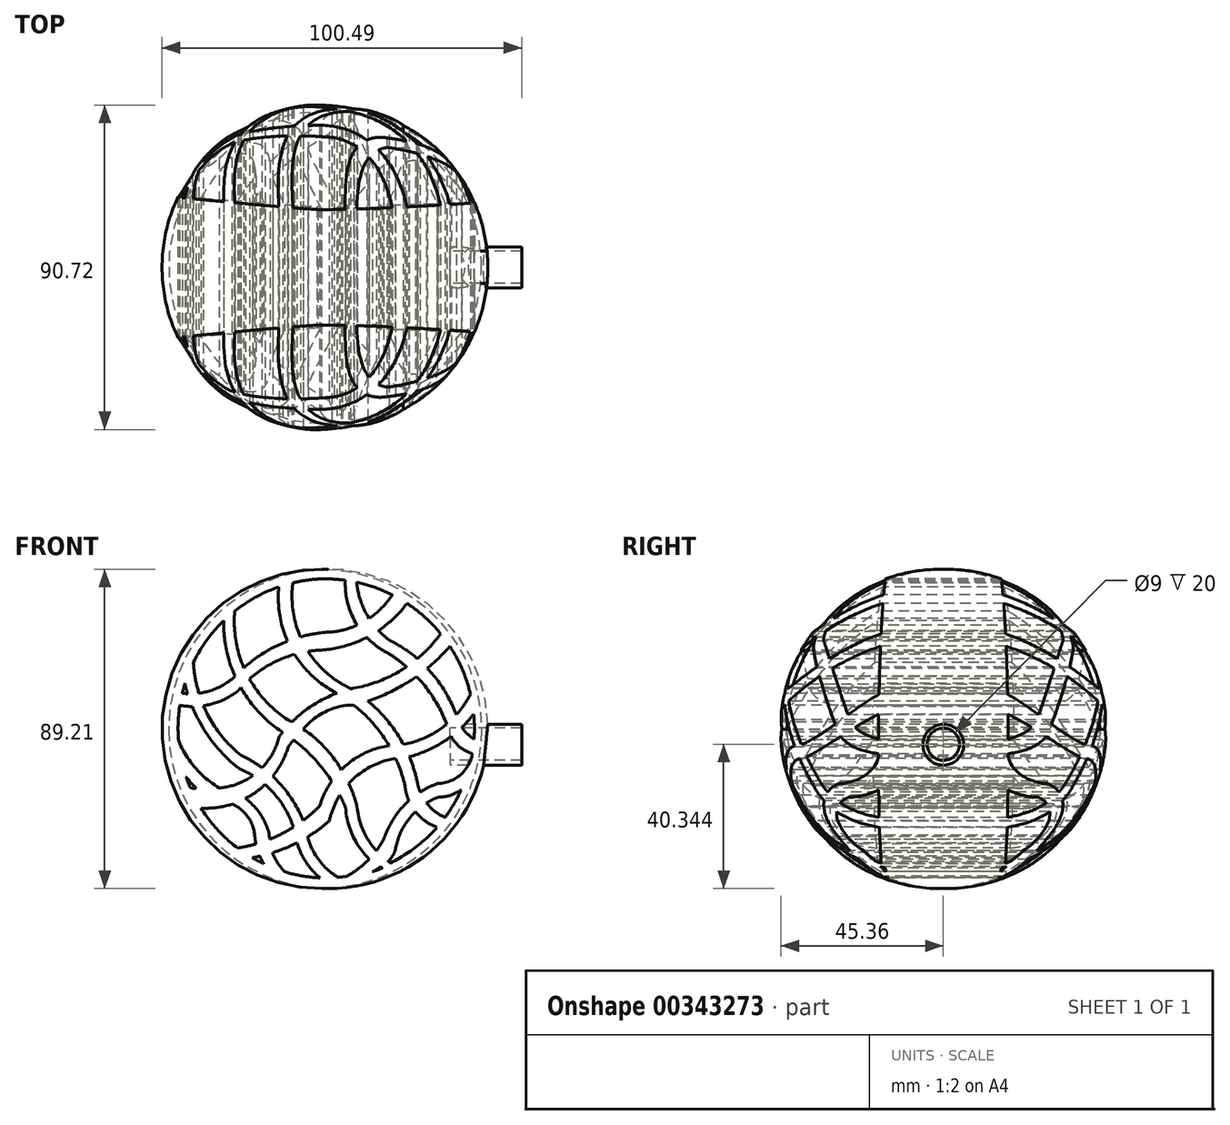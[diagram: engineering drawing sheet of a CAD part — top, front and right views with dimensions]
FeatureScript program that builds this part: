
annotation { "Feature Type Name" : "Feature", "Feature Type Description" : "" }
export const myFeature = defineFeature(function(context is Context, id is Id, definition is map)
    precondition{}
    {
        {
            var Q0;
            Q0=qCreatedBy(makeId("Front.planeOp"),FACE);
            var sketch = newSketch(context, id + "F0", { "sketchPlane" : qUnion([Q0])});
            skArc(sketch, "E0", {"start": v(-34.98, -55.53) * mm, "mid": v(10.54, -10.93) * mm, "end": v(-34.98, 33.67) * mm});
            skLineSegment(sketch, "E1", {"start": v(-34.98, 33.67) * mm, "end": v(-34.98, -55.53) * mm});
            skSolve(sketch);
        }
        {
            var Q0;
            Q0=makeQuery(id+"F0.imprint","IMPRINT",FACE,{"disambiguationData":[TD([[makeQuery(id+"F0.imprint","IMPRINT",EDGE,{"derivedFrom":sQuery(id+"F0.wireOp",EDGE,"E0")}),1.0]])]});
            var Q1;
            Q1=sQuery(id+"F0.wireOp",EDGE,"E1");
            revolve(context, id + "F1", {"entities" : qUnion([Q0]), "axis" : qUnion([Q1]), "revolveType" : RevolveType.FULL});
        }
        {
            var Q0;
            Q0=qCreatedBy(makeId("Front.planeOp"),FACE);
            var sketch = newSketch(context, id + "F2", { "sketchPlane" : qUnion([Q0])});
            skArc(sketch, "E2", {"start": v(-36.98, 31.45) * mm, "mid": v(-40.71, 31.04) * mm, "end": v(-44.39, 30.3) * mm});
            skArc(sketch, "E3", {"start": v(-37.25, -53) * mm, "mid": v(-36.08, -53.04) * mm, "end": v(-34.91, -53.06) * mm});
            skArc(sketch, "E4", {"start": v(-9.49, -26.67) * mm, "mid": v(-10.57, -22.44) * mm, "end": v(-12.1, -18.35) * mm});
            skArc(sketch, "E5", {"start": v(-9.49, -26.67) * mm, "mid": v(-9.1, -28.02) * mm, "end": v(-8.57, -29.33) * mm});
            skArc(sketch, "E6", {"start": v(-44.39, 30.3) * mm, "mid": v(-44.42, 22.07) * mm, "end": v(-42.13, 14.17) * mm});
            skPoint(sketch, "E7.end.orphan", {"position": v(-32.31, 0) * mm});
            skArc(sketch, "E8", {"start": v(-47.27, 29.48) * mm, "mid": v(-47.15, 21.22) * mm, "end": v(-44.74, 13.3) * mm});
            skArc(sketch, "E9", {"start": v(-12.1, -26.66) * mm, "mid": v(-13.32, -22.55) * mm, "end": v(-14.95, -18.58) * mm});
            skArc(sketch, "E10", {"start": v(-12.1, -26.66) * mm, "mid": v(-11.7, -28.95) * mm, "end": v(-10.9, -31.12) * mm});
            skArc(sketch, "E11", {"start": v(-60.68, 22.25) * mm, "mid": v(-60.35, 13.59) * mm, "end": v(-57.8, 5.3) * mm});
            skArc(sketch, "E12", {"start": v(-26.5, -32.73) * mm, "mid": v(-27.54, -29.33) * mm, "end": v(-28.9, -26.06) * mm});
            skArc(sketch, "E13", {"start": v(-26.5, -32.73) * mm, "mid": v(-24.64, -39.73) * mm, "end": v(-20.58, -45.73) * mm});
            skArc(sketch, "E14", {"start": v(-62.74, 20.49) * mm, "mid": v(-62.14, 11.87) * mm, "end": v(-59.5, 3.64) * mm});
            skArc(sketch, "E15", {"start": v(-28.74, -32.73) * mm, "mid": v(-29.7, -30.56) * mm, "end": v(-30.77, -28.45) * mm});
            skArc(sketch, "E16", {"start": v(-28.74, -32.73) * mm, "mid": v(-26.7, -40.64) * mm, "end": v(-21.92, -47.29) * mm});
            skArc(sketch, "E17", {"start": v(-72.25, 7.8) * mm, "mid": v(-71.71, 3.08) * mm, "end": v(-70.56, -1.51) * mm});
            skArc(sketch, "E18", {"start": v(-41.33, -37.32) * mm, "mid": v(-45.02, -30.23) * mm, "end": v(-50.3, -24.22) * mm});
            skArc(sketch, "E19", {"start": v(-40.38, -40.83) * mm, "mid": v(-37.15, -47.76) * mm, "end": v(-31.5, -52.91) * mm});
            skArc(sketch, "E20", {"start": v(-74.01, 3.64) * mm, "mid": v(-73.41, 0.99) * mm, "end": v(-72.65, -1.62) * mm});
            skArc(sketch, "E21", {"start": v(-43.21, -38.6) * mm, "mid": v(-46.54, -31.57) * mm, "end": v(-51.74, -25.78) * mm});
            skArc(sketch, "E22", {"start": v(-42.48, -42) * mm, "mid": v(-39.62, -48.16) * mm, "end": v(-34.91, -53.06) * mm});
            skArc(sketch, "E23", {"start": v(-76.4, -14.3) * mm, "mid": v(-71.65, -22.1) * mm, "end": v(-64.61, -27.94) * mm});
            skArc(sketch, "E24", {"start": v(-75.14, -21.58) * mm, "mid": v(-72.79, -24.73) * mm, "end": v(-70.07, -27.58) * mm});
            skArc(sketch, "E25", {"start": v(-51.1, -40.4) * mm, "mid": v(-53.68, -34.67) * mm, "end": v(-58.24, -30.32) * mm});
            skArc(sketch, "E26", {"start": v(-51.1, -40.4) * mm, "mid": v(-51.04, -41.45) * mm, "end": v(-50.92, -42.48) * mm});
            skArc(sketch, "E27", {"start": v(-54.11, -40.57) * mm, "mid": v(-56.23, -35.03) * mm, "end": v(-60.9, -31.4) * mm});
            skArc(sketch, "E28", {"start": v(-54.11, -40.57) * mm, "mid": v(-53.93, -42) * mm, "end": v(-53.65, -43.41) * mm});
            skArc(sketch, "E29", {"start": v(-28.76, 31.04) * mm, "mid": v(-28.08, 24.17) * mm, "end": v(-25.23, 17.88) * mm});
            skArc(sketch, "E30", {"start": v(-0.36, -9.76) * mm, "mid": v(-4.1, -2.21) * mm, "end": v(-9.3, 4.4) * mm});
            skArc(sketch, "E31", {"start": v(0.5, -12.2) * mm, "mid": v(3.02, -15.57) * mm, "end": v(6.77, -17.47) * mm});
            skArc(sketch, "E32", {"start": v(-26.71, 30.69) * mm, "mid": v(-25.48, 24.72) * mm, "end": v(-22.78, 19.26) * mm});
            skArc(sketch, "E33", {"start": v(1.51, -8) * mm, "mid": v(-2, -0.48) * mm, "end": v(-7.1, 6.07) * mm});
            skArc(sketch, "E34", {"start": v(2.63, -10.39) * mm, "mid": v(4.6, -12.8) * mm, "end": v(7.13, -14.62) * mm});
            skArc(sketch, "E35", {"start": v(-35.98, 11.62) * mm, "mid": v(-29.38, 12.78) * mm, "end": v(-23.17, 15.27) * mm});
            skArc(sketch, "E36", {"start": v(-35.98, 11.62) * mm, "mid": v(-38.26, 11.45) * mm, "end": v(-40.52, 11.12) * mm});
            skArc(sketch, "E37", {"start": v(-75.96, -3.74) * mm, "mid": v(-73.85, -4.06) * mm, "end": v(-71.73, -4.15) * mm});
            skArc(sketch, "E38", {"start": v(-32.4, 15.7) * mm, "mid": v(-28.73, 16.5) * mm, "end": v(-25.23, 17.88) * mm});
            skArc(sketch, "E39", {"start": v(-32.4, 15.7) * mm, "mid": v(-37.31, 15.24) * mm, "end": v(-42.13, 14.17) * mm});
            skArc(sketch, "E40", {"start": v(-75.5, -1.4) * mm, "mid": v(-74.07, -1.56) * mm, "end": v(-72.65, -1.62) * mm});
            skArc(sketch, "E41", {"start": v(-26.71, 0) * mm, "mid": v(-18.67, 2.33) * mm, "end": v(-11.34, 6.37) * mm});
            skArc(sketch, "E42", {"start": v(-26.71, 0) * mm, "mid": v(-27.29, -0.13) * mm, "end": v(-27.86, -0.28) * mm});
            skPoint(sketch, "E43.startSnap0", {"position": v(-71.16, -26.53) * mm});
            skArc(sketch, "E44", {"start": v(-70.56, -32.48) * mm, "mid": v(-65.67, -32.44) * mm, "end": v(-60.9, -31.4) * mm});
            skPoint(sketch, "E44.startSnap0", {"position": v(-6.54, -32.48) * mm});
            skArc(sketch, "E45", {"start": v(-26.71, -3.74) * mm, "mid": v(-26.71, -3.74) * mm, "end": v(-26.72, -3.74) * mm});
            skArc(sketch, "E46", {"start": v(-24, -2.97) * mm, "mid": v(-16.36, 0.14) * mm, "end": v(-9.3, 4.4) * mm});
            skArc(sketch, "E47", {"start": v(-59.5, -44.73) * mm, "mid": v(-56.55, -44.18) * mm, "end": v(-53.65, -43.41) * mm});
            skArc(sketch, "E48", {"start": v(-16.29, -15.99) * mm, "mid": v(-23.99, -18.32) * mm, "end": v(-30.45, -23.1) * mm});
            skArc(sketch, "E49", {"start": v(-13.32, -15.81) * mm, "mid": v(-6.43, -13.67) * mm, "end": v(-0.36, -9.76) * mm});
            skArc(sketch, "E50", {"start": v(-56.74, -46.61) * mm, "mid": v(-54.79, -46.29) * mm, "end": v(-52.85, -45.88) * mm});
            skArc(sketch, "E51", {"start": v(-14.95, -18.58) * mm, "mid": v(-22.58, -21.09) * mm, "end": v(-28.9, -26.06) * mm});
            skArc(sketch, "E52", {"start": v(-12.1, -18.35) * mm, "mid": v(-5.48, -15.95) * mm, "end": v(0.5, -12.2) * mm});
            skArc(sketch, "E53", {"start": v(-28.74, -52.6) * mm, "mid": v(-25.12, -50.22) * mm, "end": v(-21.92, -47.29) * mm});
            skPoint(sketch, "E53.endSnap0", {"position": v(-23.47, -41.94) * mm});
            skArc(sketch, "E54", {"start": v(-3.43, -26.67) * mm, "mid": v(-6.08, -27.85) * mm, "end": v(-8.57, -29.33) * mm});
            skArc(sketch, "E55", {"start": v(-3.43, -26.67) * mm, "mid": v(3.39, -23.97) * mm, "end": v(6.77, -17.47) * mm});
            skArc(sketch, "E56", {"start": v(-23.86, -51.57) * mm, "mid": v(-21.54, -50.67) * mm, "end": v(-19.44, -49.34) * mm});
            skArc(sketch, "E57", {"start": v(-3.43, -29.49) * mm, "mid": v(-5.43, -30.38) * mm, "end": v(-7.32, -31.48) * mm});
            skArc(sketch, "E58", {"start": v(-3.43, -29.49) * mm, "mid": v(0.88, -28.62) * mm, "end": v(4.45, -26.05) * mm});
            skArc(sketch, "E59.trimOffspring", {"start": v(-43.24, 10.5) * mm, "mid": v(-38.46, 4.54) * mm, "end": v(-32.31, 0) * mm});
            skArc(sketch, "E60.trimOffspring", {"start": v(-44.74, 13.3) * mm, "mid": v(-51.66, 9.95) * mm, "end": v(-57.8, 5.3) * mm});
            skArc(sketch, "E61.trimOffspring", {"start": v(-40.52, 11.12) * mm, "mid": v(-36.04, 5.47) * mm, "end": v(-30.3, 1.1) * mm});
            skArc(sketch, "E62.trimOffspring", {"start": v(-43.24, 10.5) * mm, "mid": v(-50.4, 7.61) * mm, "end": v(-56.7, 3.12) * mm});
            skArc(sketch, "E63.trimOffspring", {"start": v(-30.5, -1.07) * mm, "mid": v(-37.79, -4.56) * mm, "end": v(-44.1, -9.6) * mm});
            skArc(sketch, "E64.trimOffspring", {"start": v(-27.86, -0.28) * mm, "mid": v(-29.07, 0.43) * mm, "end": v(-30.3, 1.1) * mm});
            skArc(sketch, "E65.trimOffspring", {"start": v(-30.5, -1.07) * mm, "mid": v(-31.4, -0.52) * mm, "end": v(-32.31, 0) * mm});
            skArc(sketch, "E66.trimOffspring", {"start": v(-11.34, 6.37) * mm, "mid": v(-14.3, 8.77) * mm, "end": v(-17.45, 10.89) * mm});
            skArc(sketch, "E67.trimOffspring", {"start": v(-9.16, 8.02) * mm, "mid": v(-13.12, 11.06) * mm, "end": v(-17.45, 13.54) * mm});
            skArc(sketch, "E68.trimOffspring", {"start": v(-9.16, 8.02) * mm, "mid": v(-5.32, 11.62) * mm, "end": v(-2.02, 15.7) * mm});
            skArc(sketch, "E69.trimOffspring", {"start": v(-7.1, 6.07) * mm, "mid": v(-3.39, 9.36) * mm, "end": v(0, 12.98) * mm});
            skArc(sketch, "E70.trimOffspring", {"start": v(-23.17, 15.27) * mm, "mid": v(-20.5, 12.84) * mm, "end": v(-17.45, 10.89) * mm});
            skArc(sketch, "E71.trimOffspring", {"start": v(-22.78, 19.26) * mm, "mid": v(-18.95, 22.31) * mm, "end": v(-15.83, 26.08) * mm});
            skArc(sketch, "E72.trimOffspring", {"start": v(-20.8, 16.67) * mm, "mid": v(-19.2, 15.02) * mm, "end": v(-17.45, 13.54) * mm});
            skArc(sketch, "E73.trimOffspring", {"start": v(-20.8, 16.67) * mm, "mid": v(-16.1, 20.34) * mm, "end": v(-12.17, 24.82) * mm});
            skLineSegment(sketch, "E74", {"start": v(-15.83, 26.08) * mm, "end": v(-15.42, 26.7) * mm});
            skArc(sketch, "E75.trimOffspring", {"start": v(-28.76, 31.04) * mm, "mid": v(-32.86, 31.45) * mm, "end": v(-36.98, 31.45) * mm});
            skArc(sketch, "E76.trimOffspring", {"start": v(-15.42, 26.7) * mm, "mid": v(-20.92, 29.1) * mm, "end": v(-26.71, 30.69) * mm});
            skArc(sketch, "E77.trimOffspring", {"start": v(-2.02, 15.7) * mm, "mid": v(-6.72, 20.68) * mm, "end": v(-12.17, 24.82) * mm});
            skArc(sketch, "E78.trimOffspring", {"start": v(-47.27, 29.48) * mm, "mid": v(-54.3, 26.48) * mm, "end": v(-60.68, 22.25) * mm});
            skArc(sketch, "E79.trimOffspring", {"start": v(-62.74, 20.49) * mm, "mid": v(-68.1, 14.6) * mm, "end": v(-72.25, 7.8) * mm});
            skArc(sketch, "E80.trimOffspring", {"start": v(-74.01, 3.64) * mm, "mid": v(-74.83, 1.14) * mm, "end": v(-75.5, -1.4) * mm});
            skArc(sketch, "E81.trimOffspring", {"start": v(6.22, -1.28) * mm, "mid": v(3.77, 6.14) * mm, "end": v(0, 12.98) * mm});
            skArc(sketch, "E82.trimOffspring", {"start": v(2.63, -10.39) * mm, "mid": v(4.92, -8.04) * mm, "end": v(6.97, -5.48) * mm});
            skPoint(sketch, "E83.orphan", {"position": v(0, -10.77) * mm});
            skArc(sketch, "E84.trimOffspring", {"start": v(1.51, -8) * mm, "mid": v(4.13, -4.82) * mm, "end": v(6.22, -1.28) * mm});
            skArc(sketch, "E85.trimOffspring", {"start": v(6.6, -18.46) * mm, "mid": v(6.69, -17.96) * mm, "end": v(6.77, -17.47) * mm});
            skArc(sketch, "E86.trimOffspring", {"start": v(7.13, -14.62) * mm, "mid": v(7.3, -10.05) * mm, "end": v(6.97, -5.48) * mm});
            skArc(sketch, "E87.trimOffspring", {"start": v(-13.32, -15.81) * mm, "mid": v(-17.99, -8.83) * mm, "end": v(-24, -2.97) * mm});
            skArc(sketch, "E88.trimOffspring", {"start": v(-16.29, -15.99) * mm, "mid": v(-20.9, -9.36) * mm, "end": v(-26.72, -3.74) * mm});
            skArc(sketch, "E89.trimOffspring", {"start": v(-64.61, -27.94) * mm, "mid": v(-59.13, -26.7) * mm, "end": v(-54.23, -23.94) * mm});
            skPoint(sketch, "E43.start.orphan", {"position": v(-73.5, -26.53) * mm});
            skArc(sketch, "E90.trimOffspring", {"start": v(-58.24, -30.32) * mm, "mid": v(-54.8, -28.33) * mm, "end": v(-51.74, -25.78) * mm});
            skArc(sketch, "E91", {"start": v(-73.06, -27.58) * mm, "mid": v(-71.57, -28.05) * mm, "end": v(-70.07, -27.58) * mm});
            skArc(sketch, "E92.trimOffspring", {"start": v(-75.14, -21.58) * mm, "mid": v(-74.22, -24.62) * mm, "end": v(-73.06, -27.58) * mm});
            skArc(sketch, "E93.trimOffspring", {"start": v(-52.85, -45.88) * mm, "mid": v(-51.9, -47.88) * mm, "end": v(-50.7, -49.76) * mm});
            skArc(sketch, "E94.trimOffspring", {"start": v(-50.92, -42.48) * mm, "mid": v(-46.96, -40.74) * mm, "end": v(-43.21, -38.6) * mm});
            skArc(sketch, "E95.trimOffspring", {"start": v(-50.26, -45.18) * mm, "mid": v(-48.72, -48.45) * mm, "end": v(-46.49, -51.29) * mm});
            skArc(sketch, "E96.trimOffspring", {"start": v(-50.26, -45.18) * mm, "mid": v(-46.3, -43.78) * mm, "end": v(-42.48, -42) * mm});
            skArc(sketch, "E97.trimOffspring", {"start": v(-56.74, -46.61) * mm, "mid": v(-53.79, -48.3) * mm, "end": v(-50.7, -49.76) * mm});
            skPoint(sketch, "E98.orphan", {"position": v(-43.06, -39.1) * mm});
            skArc(sketch, "E99.trimOffspring", {"start": v(-41.33, -37.32) * mm, "mid": v(-38.56, -35.14) * mm, "end": v(-35.98, -32.73) * mm});
            skPoint(sketch, "E100.orphan", {"position": v(-40.72, -39.1) * mm});
            skArc(sketch, "E101.trimOffspring", {"start": v(-40.38, -40.83) * mm, "mid": v(-37.2, -38.74) * mm, "end": v(-34.22, -36.38) * mm});
            skArc(sketch, "E102.trimOffspring", {"start": v(-69.65, -4.02) * mm, "mid": v(-65.13, -12.08) * mm, "end": v(-58.73, -18.73) * mm});
            skArc(sketch, "E103.trimOffspring", {"start": v(-69.65, -4.02) * mm, "mid": v(-64.4, -2.69) * mm, "end": v(-59.7, 0) * mm});
            skArc(sketch, "E104.trimOffspring", {"start": v(-71.73, -4.15) * mm, "mid": v(-66.36, -13.71) * mm, "end": v(-58.73, -21.58) * mm});
            skArc(sketch, "E105.trimOffspring", {"start": v(-70.56, -1.51) * mm, "mid": v(-64.6, 0.15) * mm, "end": v(-59.5, 3.64) * mm});
            skArc(sketch, "E106.trimOffspring", {"start": v(-58.4, 1.45) * mm, "mid": v(-53.66, -5.3) * mm, "end": v(-47.52, -10.78) * mm});
            skArc(sketch, "E107.trimOffspring", {"start": v(-58.4, 1.45) * mm, "mid": v(-59.06, 0.73) * mm, "end": v(-59.7, 0) * mm});
            skArc(sketch, "E108.trimOffspring", {"start": v(-56.7, 3.12) * mm, "mid": v(-51.88, -3.54) * mm, "end": v(-45.58, -8.8) * mm});
            skArc(sketch, "E109.trimOffspring", {"start": v(-18, -48.03) * mm, "mid": v(-16.8, -46.51) * mm, "end": v(-15.83, -44.83) * mm});
            skArc(sketch, "E110.trimOffspring", {"start": v(-16.74, -48.92) * mm, "mid": v(-9.2, -44.28) * mm, "end": v(-2.78, -38.18) * mm});
            skArc(sketch, "E111.trimOffspring", {"start": v(-18, -48.03) * mm, "mid": v(-17.38, -48.49) * mm, "end": v(-16.74, -48.92) * mm});
            skArc(sketch, "E112.trimOffspring", {"start": v(-20.58, -45.73) * mm, "mid": v(-19.24, -43.89) * mm, "end": v(-18.06, -41.94) * mm});
            skArc(sketch, "E113.trimOffspring", {"start": v(-19.44, -49.34) * mm, "mid": v(-19.1, -49.58) * mm, "end": v(-18.74, -49.82) * mm});
            skArc(sketch, "E114.trimOffspring", {"start": v(-30.77, -28.45) * mm, "mid": v(-32.87, -32.26) * mm, "end": v(-34.22, -36.38) * mm});
            skArc(sketch, "E115.trimOffspring", {"start": v(-30.45, -23.1) * mm, "mid": v(-35.4, -16.47) * mm, "end": v(-41.71, -11.1) * mm});
            skArc(sketch, "E116.trimOffspring", {"start": v(-32.48, -25.55) * mm, "mid": v(-34.54, -28.99) * mm, "end": v(-35.98, -32.73) * mm});
            skArc(sketch, "E117.trimOffspring", {"start": v(-32.48, -25.55) * mm, "mid": v(-37.6, -18.92) * mm, "end": v(-43.81, -13.3) * mm});
            skArc(sketch, "E118.trimOffspring", {"start": v(-31.5, -52.91) * mm, "mid": v(-30.11, -52.77) * mm, "end": v(-28.74, -52.6) * mm});
            skArc(sketch, "E119.trimOffspring", {"start": v(-46.49, -51.29) * mm, "mid": v(-41.92, -52.4) * mm, "end": v(-37.25, -53) * mm});
            skArc(sketch, "E120.trimOffspring", {"start": v(-9.63, -33.28) * mm, "mid": v(-6.6, -36.29) * mm, "end": v(-2.78, -38.18) * mm});
            skArc(sketch, "E121.trimOffspring", {"start": v(-9.63, -33.28) * mm, "mid": v(-13.73, -38.52) * mm, "end": v(-15.83, -44.83) * mm});
            skArc(sketch, "E122.trimOffspring", {"start": v(-7.32, -31.48) * mm, "mid": v(-4.63, -34.31) * mm, "end": v(-1.24, -36.26) * mm});
            skArc(sketch, "E123.trimOffspring", {"start": v(-10.9, -31.12) * mm, "mid": v(-15.21, -36.05) * mm, "end": v(-18.06, -41.94) * mm});
            skArc(sketch, "E124.trimOffspring", {"start": v(-75.96, -3.74) * mm, "mid": v(-76.5, -9) * mm, "end": v(-76.4, -14.3) * mm});
            skArc(sketch, "E125.trimOffspring", {"start": v(-44.1, -9.6) * mm, "mid": v(-44.84, -9.2) * mm, "end": v(-45.58, -8.8) * mm});
            skArc(sketch, "E126.trimOffspring", {"start": v(-43.81, -13.3) * mm, "mid": v(-44.8, -14.53) * mm, "end": v(-45.73, -15.81) * mm});
            skArc(sketch, "E127.trimOffspring", {"start": v(-46.03, -11.73) * mm, "mid": v(-46.77, -11.25) * mm, "end": v(-47.52, -10.78) * mm});
            skArc(sketch, "E128.trimOffspring", {"start": v(-46.03, -11.73) * mm, "mid": v(-46.66, -12.5) * mm, "end": v(-47.27, -13.28) * mm});
            skArc(sketch, "E129", {"start": v(-26.71, -3.74) * mm, "mid": v(-35.08, -5.64) * mm, "end": v(-41.71, -11.1) * mm});
            skArc(sketch, "E130.trimOffspring", {"start": v(-1.24, -36.26) * mm, "mid": v(1.96, -31.35) * mm, "end": v(4.45, -26.05) * mm});
            skArc(sketch, "E131.trimOffspring", {"start": v(-52.49, -22.42) * mm, "mid": v(-49.24, -18.21) * mm, "end": v(-47.27, -13.28) * mm});
            skArc(sketch, "E132.trimOffspring", {"start": v(-52.49, -22.42) * mm, "mid": v(-55.5, -20.4) * mm, "end": v(-58.73, -18.73) * mm});
            skArc(sketch, "E133.trimOffspring", {"start": v(-50.3, -24.22) * mm, "mid": v(-47.58, -20.25) * mm, "end": v(-45.73, -15.81) * mm});
            skArc(sketch, "E134.trimOffspring", {"start": v(-54.23, -23.94) * mm, "mid": v(-56.42, -22.65) * mm, "end": v(-58.73, -21.58) * mm});
            skArc(sketch, "E135.trimOffspring", {"start": v(-70.56, -32.48) * mm, "mid": v(-65.63, -39.15) * mm, "end": v(-59.5, -44.73) * mm});
            skArc(sketch, "E136.trimOffspring", {"start": v(-23.86, -51.57) * mm, "mid": v(-21.27, -50.77) * mm, "end": v(-18.74, -49.82) * mm});
            skSolve(sketch);
        }
        {
            var Q0;
            Q0=qCreatedBy(makeId("Front.planeOp"),FACE);
            var sketch = newSketch(context, id + "F3", { "sketchPlane" : qUnion([Q0])});
            skArc(sketch, "E137.0", {"start": v(-36.95, 30.95) * mm, "mid": v(-40.47, 30.57) * mm, "end": v(-43.94, 29.9) * mm});
            skArc(sketch, "E137.1", {"start": v(-32.45, 16.21) * mm, "mid": v(-37.19, 15.78) * mm, "end": v(-41.84, 14.78) * mm});
            skArc(sketch, "E137.2", {"start": v(-32.45, 16.21) * mm, "mid": v(-29.14, 16.92) * mm, "end": v(-25.97, 18.1) * mm});
            skArc(sketch, "E137.3", {"start": v(-43.94, 29.9) * mm, "mid": v(-43.92, 22.2) * mm, "end": v(-41.84, 14.78) * mm});
            skArc(sketch, "E137.4", {"start": v(-29.3, 30.6) * mm, "mid": v(-28.58, 24.1) * mm, "end": v(-25.97, 18.1) * mm});
            skArc(sketch, "E137.5", {"start": v(-29.3, 30.6) * mm, "mid": v(-33.11, 30.95) * mm, "end": v(-36.95, 30.95) * mm});
            skArc(sketch, "E138.0", {"start": v(-26.14, 30.05) * mm, "mid": v(-24.97, 24.8) * mm, "end": v(-22.63, 19.96) * mm});
            skArc(sketch, "E138.1", {"start": v(-16.16, 26.51) * mm, "mid": v(-21.04, 28.6) * mm, "end": v(-26.14, 30.05) * mm});
            skLineSegment(sketch, "E138.2", {"start": v(-16.26, 26.37) * mm, "end": v(-16.16, 26.51) * mm});
            skArc(sketch, "E138.3", {"start": v(-22.63, 19.96) * mm, "mid": v(-19.13, 22.85) * mm, "end": v(-16.26, 26.37) * mm});
            skArc(sketch, "E139.0", {"start": v(-2.65, 15.68) * mm, "mid": v(-7.03, 20.27) * mm, "end": v(-12.04, 24.14) * mm});
            skArc(sketch, "E139.1", {"start": v(-20.02, 16.57) * mm, "mid": v(-15.71, 20.01) * mm, "end": v(-12.04, 24.14) * mm});
            skArc(sketch, "E139.2", {"start": v(-9.15, 8.69) * mm, "mid": v(-5.68, 11.98) * mm, "end": v(-2.65, 15.68) * mm});
            skArc(sketch, "E139.3", {"start": v(-9.15, 8.69) * mm, "mid": v(-13, 11.59) * mm, "end": v(-17.18, 13.97) * mm});
            skArc(sketch, "E139.4", {"start": v(-20.02, 16.57) * mm, "mid": v(-18.65, 15.21) * mm, "end": v(-17.18, 13.97) * mm});
            skArc(sketch, "E140.0", {"start": v(-35.95, 11.1) * mm, "mid": v(-29.43, 12.23) * mm, "end": v(-23.28, 14.65) * mm});
            skArc(sketch, "E140.1", {"start": v(-35.95, 11.1) * mm, "mid": v(-37.83, 10.98) * mm, "end": v(-39.69, 10.74) * mm});
            skArc(sketch, "E140.2", {"start": v(-23.28, 14.65) * mm, "mid": v(-20.66, 12.32) * mm, "end": v(-17.7, 10.45) * mm});
            skArc(sketch, "E140.3", {"start": v(-39.69, 10.74) * mm, "mid": v(-35.42, 5.57) * mm, "end": v(-30.06, 1.55) * mm});
            skArc(sketch, "E140.4", {"start": v(-12.16, 6.41) * mm, "mid": v(-14.85, 8.55) * mm, "end": v(-17.7, 10.45) * mm});
            skArc(sketch, "E140.5", {"start": v(-26.8, 0.5) * mm, "mid": v(-19.17, 2.68) * mm, "end": v(-12.16, 6.41) * mm});
            skArc(sketch, "E140.6", {"start": v(-26.8, 0.5) * mm, "mid": v(-27.3, 0.39) * mm, "end": v(-27.78, 0.27) * mm});
            skArc(sketch, "E140.7", {"start": v(-27.78, 0.27) * mm, "mid": v(-28.9, 0.93) * mm, "end": v(-30.06, 1.55) * mm});
            skArc(sketch, "E141.0", {"start": v(-47.86, 28.75) * mm, "mid": v(-47.63, 21.01) * mm, "end": v(-45.43, 13.6) * mm});
            skArc(sketch, "E141.1", {"start": v(-47.86, 28.75) * mm, "mid": v(-54.31, 25.9) * mm, "end": v(-60.2, 22) * mm});
            skArc(sketch, "E141.2", {"start": v(-60.2, 22) * mm, "mid": v(-59.9, 13.91) * mm, "end": v(-57.62, 6.15) * mm});
            skArc(sketch, "E141.3", {"start": v(-45.43, 13.6) * mm, "mid": v(-51.86, 10.43) * mm, "end": v(-57.62, 6.15) * mm});
            skArc(sketch, "E142.0", {"start": v(-43.47, 9.91) * mm, "mid": v(-50.15, 7.17) * mm, "end": v(-56.06, 3.01) * mm});
            skArc(sketch, "E142.1", {"start": v(-31.67, -0.96) * mm, "mid": v(-32.11, -0.7) * mm, "end": v(-32.56, -0.44) * mm});
            skArc(sketch, "E142.2", {"start": v(-31.67, -0.96) * mm, "mid": v(-38.35, -4.31) * mm, "end": v(-44.18, -8.98) * mm});
            skArc(sketch, "E142.3", {"start": v(-43.47, 9.91) * mm, "mid": v(-38.68, 4.04) * mm, "end": v(-32.56, -0.44) * mm});
            skArc(sketch, "E142.4", {"start": v(-44.18, -8.98) * mm, "mid": v(-44.75, -8.67) * mm, "end": v(-45.33, -8.37) * mm});
            skArc(sketch, "E142.5", {"start": v(-56.06, 3.01) * mm, "mid": v(-51.38, -3.33) * mm, "end": v(-45.33, -8.37) * mm});
            skArc(sketch, "E143.0", {"start": v(-26.9, -4.25) * mm, "mid": v(-34.7, -6.02) * mm, "end": v(-40.98, -10.98) * mm});
            skArc(sketch, "E143.1", {"start": v(-17.1, -15.59) * mm, "mid": v(-21.48, -9.47) * mm, "end": v(-26.9, -4.25) * mm});
            skArc(sketch, "E143.2", {"start": v(-17.1, -15.59) * mm, "mid": v(-24.26, -17.88) * mm, "end": v(-30.35, -22.28) * mm});
            skArc(sketch, "E143.3", {"start": v(-30.35, -22.28) * mm, "mid": v(-35.08, -16.08) * mm, "end": v(-40.98, -10.98) * mm});
            skArc(sketch, "E144.0", {"start": v(-13.05, -15.25) * mm, "mid": v(-17.41, -8.72) * mm, "end": v(-22.96, -3.16) * mm});
            skArc(sketch, "E144.1", {"start": v(-13.05, -15.25) * mm, "mid": v(-6.64, -13.2) * mm, "end": v(-0.96, -9.6) * mm});
            skArc(sketch, "E144.2", {"start": v(-0.96, -9.6) * mm, "mid": v(-4.5, -2.52) * mm, "end": v(-9.36, 3.74) * mm});
            skArc(sketch, "E144.3", {"start": v(-22.96, -3.16) * mm, "mid": v(-15.9, -0.2) * mm, "end": v(-9.36, 3.74) * mm});
            skArc(sketch, "E145.0", {"start": v(-6.35, 6.03) * mm, "mid": v(-3.07, 8.95) * mm, "end": v(-0.05, 12.14) * mm});
            skArc(sketch, "E145.1", {"start": v(1.71, -7.03) * mm, "mid": v(-1.65, -0.09) * mm, "end": v(-6.35, 6.03) * mm});
            skArc(sketch, "E145.2", {"start": v(1.71, -7.03) * mm, "mid": v(3.9, -4.26) * mm, "end": v(5.69, -1.22) * mm});
            skArc(sketch, "E145.3", {"start": v(5.69, -1.22) * mm, "mid": v(3.4, 5.71) * mm, "end": v(-0.05, 12.14) * mm});
            skArc(sketch, "E146.0", {"start": v(3.29, -10.47) * mm, "mid": v(4.8, -12.3) * mm, "end": v(6.69, -13.78) * mm});
            skArc(sketch, "E146.1", {"start": v(3.29, -10.47) * mm, "mid": v(5.01, -8.7) * mm, "end": v(6.6, -6.8) * mm});
            skArc(sketch, "E146.2", {"start": v(6.69, -13.78) * mm, "mid": v(6.8, -10.3) * mm, "end": v(6.6, -6.8) * mm});
            skArc(sketch, "E147.0", {"start": v(-11.4, -18.7) * mm, "mid": v(-5.27, -16.4) * mm, "end": v(0.31, -13) * mm});
            skArc(sketch, "E147.1", {"start": v(-3.52, -26.16) * mm, "mid": v(2.85, -23.76) * mm, "end": v(6.2, -17.84) * mm});
            skArc(sketch, "E147.2", {"start": v(-3.52, -26.16) * mm, "mid": v(-6, -27.24) * mm, "end": v(-8.35, -28.57) * mm});
            skArc(sketch, "E147.3", {"start": v(0.31, -13) * mm, "mid": v(2.76, -16.01) * mm, "end": v(6.2, -17.84) * mm});
            skArc(sketch, "E147.4", {"start": v(-8.99, -26.56) * mm, "mid": v(-8.7, -27.58) * mm, "end": v(-8.35, -28.57) * mm});
            skArc(sketch, "E147.5", {"start": v(-8.99, -26.56) * mm, "mid": v(-10, -22.57) * mm, "end": v(-11.4, -18.7) * mm});
            skArc(sketch, "E148.0", {"start": v(-3.33, -30) * mm, "mid": v(-5, -30.73) * mm, "end": v(-6.6, -31.62) * mm});
            skArc(sketch, "E148.1", {"start": v(-3.33, -30) * mm, "mid": v(0.05, -29.47) * mm, "end": v(3.11, -27.93) * mm});
            skArc(sketch, "E148.2", {"start": v(-1.4, -35.64) * mm, "mid": v(1.06, -31.9) * mm, "end": v(3.11, -27.93) * mm});
            skArc(sketch, "E148.3", {"start": v(-6.6, -31.62) * mm, "mid": v(-4.26, -33.96) * mm, "end": v(-1.4, -35.64) * mm});
            skArc(sketch, "E149.0", {"start": v(-12.6, -26.74) * mm, "mid": v(-13.74, -22.88) * mm, "end": v(-15.25, -19.14) * mm});
            skArc(sketch, "E149.1", {"start": v(-12.6, -26.74) * mm, "mid": v(-12.23, -28.91) * mm, "end": v(-11.52, -31) * mm});
            skArc(sketch, "E149.2", {"start": v(-26, -32.64) * mm, "mid": v(-27, -29.34) * mm, "end": v(-28.3, -26.15) * mm});
            skArc(sketch, "E149.3", {"start": v(-26, -32.64) * mm, "mid": v(-24.3, -39.23) * mm, "end": v(-20.61, -44.94) * mm});
            skArc(sketch, "E149.4", {"start": v(-20.61, -44.94) * mm, "mid": v(-19.51, -43.38) * mm, "end": v(-18.52, -41.73) * mm});
            skArc(sketch, "E149.5", {"start": v(-15.25, -19.14) * mm, "mid": v(-22.36, -21.55) * mm, "end": v(-28.3, -26.15) * mm});
            skArc(sketch, "E149.6", {"start": v(-11.52, -31) * mm, "mid": v(-15.73, -35.9) * mm, "end": v(-18.52, -41.73) * mm});
            skArc(sketch, "E150.0", {"start": v(-17.26, -47.95) * mm, "mid": v(-16.2, -46.53) * mm, "end": v(-15.34, -44.98) * mm});
            skArc(sketch, "E150.1", {"start": v(-9.7, -34.03) * mm, "mid": v(-13.43, -39.03) * mm, "end": v(-15.34, -44.98) * mm});
            skArc(sketch, "E150.2", {"start": v(-17.26, -47.95) * mm, "mid": v(-16.98, -48.15) * mm, "end": v(-16.7, -48.34) * mm});
            skArc(sketch, "E150.3", {"start": v(-16.7, -48.34) * mm, "mid": v(-9.69, -44.02) * mm, "end": v(-3.66, -38.42) * mm});
            skArc(sketch, "E150.4", {"start": v(-9.7, -34.03) * mm, "mid": v(-6.98, -36.64) * mm, "end": v(-3.66, -38.42) * mm});
            skArc(sketch, "E151.0", {"start": v(-63.3, 19.28) * mm, "mid": v(-68.01, 13.85) * mm, "end": v(-71.74, 7.69) * mm});
            skArc(sketch, "E151.1", {"start": v(-63.3, 19.28) * mm, "mid": v(-62.55, 11.34) * mm, "end": v(-60.1, 3.76) * mm});
            skArc(sketch, "E151.2", {"start": v(-70.2, -0.96) * mm, "mid": v(-64.79, 0.62) * mm, "end": v(-60.1, 3.76) * mm});
            skArc(sketch, "E151.3", {"start": v(-71.74, 7.69) * mm, "mid": v(-71.24, 3.32) * mm, "end": v(-70.2, -0.96) * mm});
            skArc(sketch, "E152.0", {"start": v(-74.12, 1.73) * mm, "mid": v(-73.76, 0.3) * mm, "end": v(-73.35, -1.1) * mm});
            skArc(sketch, "E152.1", {"start": v(-74.12, 1.73) * mm, "mid": v(-74.52, 0.38) * mm, "end": v(-74.87, -0.97) * mm});
            skArc(sketch, "E152.2", {"start": v(-74.87, -0.97) * mm, "mid": v(-74.11, -1.05) * mm, "end": v(-73.35, -1.1) * mm});
            skArc(sketch, "E153.0", {"start": v(-19.44, -49.44) * mm, "mid": v(-19.17, -49.62) * mm, "end": v(-18.9, -49.8) * mm});
            skArc(sketch, "E153.1", {"start": v(-21.7, -50.84) * mm, "mid": v(-20.53, -50.2) * mm, "end": v(-19.44, -49.44) * mm});
            skArc(sketch, "E153.2", {"start": v(-21.7, -50.84) * mm, "mid": v(-20.3, -50.34) * mm, "end": v(-18.9, -49.8) * mm});
            skArc(sketch, "E154.0", {"start": v(-58.5, 0.6) * mm, "mid": v(-58.93, 0.11) * mm, "end": v(-59.34, -0.37) * mm});
            skArc(sketch, "E154.1", {"start": v(-68.93, -4.44) * mm, "mid": v(-63.87, -3.02) * mm, "end": v(-59.34, -0.37) * mm});
            skArc(sketch, "E154.2", {"start": v(-58.5, 0.6) * mm, "mid": v(-53.8, -5.9) * mm, "end": v(-47.8, -11.2) * mm});
            skArc(sketch, "E154.3", {"start": v(-68.93, -4.44) * mm, "mid": v(-64.55, -12.01) * mm, "end": v(-58.46, -18.3) * mm});
            skArc(sketch, "E154.4", {"start": v(-46.79, -11.84) * mm, "mid": v(-47.29, -11.52) * mm, "end": v(-47.8, -11.2) * mm});
            skArc(sketch, "E154.5", {"start": v(-46.79, -11.84) * mm, "mid": v(-47.27, -12.44) * mm, "end": v(-47.74, -13.05) * mm});
            skArc(sketch, "E154.6", {"start": v(-52.54, -21.75) * mm, "mid": v(-49.55, -17.72) * mm, "end": v(-47.74, -13.05) * mm});
            skArc(sketch, "E154.7", {"start": v(-52.54, -21.75) * mm, "mid": v(-55.41, -19.87) * mm, "end": v(-58.46, -18.3) * mm});
            skArc(sketch, "E155.0", {"start": v(-75.54, -4.34) * mm, "mid": v(-76, -9.25) * mm, "end": v(-75.9, -14.18) * mm});
            skArc(sketch, "E155.1", {"start": v(-72.07, -4.66) * mm, "mid": v(-66.65, -14.18) * mm, "end": v(-58.99, -22.02) * mm});
            skArc(sketch, "E155.2", {"start": v(-55.12, -23.98) * mm, "mid": v(-57.02, -22.92) * mm, "end": v(-58.99, -22.02) * mm});
            skArc(sketch, "E155.3", {"start": v(-75.54, -4.34) * mm, "mid": v(-73.8, -4.57) * mm, "end": v(-72.07, -4.66) * mm});
            skArc(sketch, "E155.4", {"start": v(-64.5, -27.42) * mm, "mid": v(-59.58, -26.33) * mm, "end": v(-55.12, -23.98) * mm});
            skArc(sketch, "E155.5", {"start": v(-75.9, -14.18) * mm, "mid": v(-71.29, -21.74) * mm, "end": v(-64.5, -27.42) * mm});
            skArc(sketch, "E156.0", {"start": v(-33.1, -25.54) * mm, "mid": v(-37.92, -19.31) * mm, "end": v(-43.74, -14) * mm});
            skArc(sketch, "E156.1", {"start": v(-49.6, -24.17) * mm, "mid": v(-47.04, -20.31) * mm, "end": v(-45.27, -16.04) * mm});
            skArc(sketch, "E156.2", {"start": v(-41.1, -36.52) * mm, "mid": v(-44.65, -29.87) * mm, "end": v(-49.6, -24.17) * mm});
            skArc(sketch, "E156.3", {"start": v(-43.74, -14) * mm, "mid": v(-44.53, -15) * mm, "end": v(-45.27, -16.04) * mm});
            skArc(sketch, "E156.4", {"start": v(-41.1, -36.52) * mm, "mid": v(-38.69, -34.58) * mm, "end": v(-36.43, -32.46) * mm});
            skArc(sketch, "E156.5", {"start": v(-33.1, -25.54) * mm, "mid": v(-35.04, -28.86) * mm, "end": v(-36.43, -32.46) * mm});
            skArc(sketch, "E157.0", {"start": v(-57.23, -30.4) * mm, "mid": v(-54.33, -28.62) * mm, "end": v(-51.71, -26.46) * mm});
            skArc(sketch, "E157.1", {"start": v(-50.34, -41.71) * mm, "mid": v(-52.63, -35.35) * mm, "end": v(-57.23, -30.4) * mm});
            skArc(sketch, "E157.2", {"start": v(-50.34, -41.71) * mm, "mid": v(-47, -40.2) * mm, "end": v(-43.81, -38.38) * mm});
            skArc(sketch, "E157.3", {"start": v(-43.81, -38.38) * mm, "mid": v(-46.94, -31.88) * mm, "end": v(-51.71, -26.46) * mm});
            skArc(sketch, "E158.0", {"start": v(-73.78, -24.32) * mm, "mid": v(-72.42, -25.93) * mm, "end": v(-70.95, -27.45) * mm});
            skArc(sketch, "E158.1", {"start": v(-73.78, -24.32) * mm, "mid": v(-73.25, -25.8) * mm, "end": v(-72.66, -27.24) * mm});
            skArc(sketch, "E158.2", {"start": v(-72.66, -27.24) * mm, "mid": v(-71.83, -27.52) * mm, "end": v(-70.95, -27.45) * mm});
            skArc(sketch, "E159.0", {"start": v(-54.62, -40.61) * mm, "mid": v(-56.58, -35.4) * mm, "end": v(-60.92, -31.93) * mm});
            skArc(sketch, "E159.1", {"start": v(-69.6, -33.06) * mm, "mid": v(-65.21, -32.9) * mm, "end": v(-60.92, -31.93) * mm});
            skArc(sketch, "E159.2", {"start": v(-54.62, -40.61) * mm, "mid": v(-54.47, -41.84) * mm, "end": v(-54.25, -43.06) * mm});
            skArc(sketch, "E159.3", {"start": v(-59.36, -44.2) * mm, "mid": v(-56.79, -43.7) * mm, "end": v(-54.25, -43.06) * mm});
            skArc(sketch, "E159.4", {"start": v(-69.6, -33.06) * mm, "mid": v(-65, -39.1) * mm, "end": v(-59.36, -44.2) * mm});
            skArc(sketch, "E160.0", {"start": v(-29.24, -32.84) * mm, "mid": v(-30, -31.13) * mm, "end": v(-30.82, -29.45) * mm});
            skArc(sketch, "E160.1", {"start": v(-29.24, -32.84) * mm, "mid": v(-27.24, -40.67) * mm, "end": v(-22.64, -47.3) * mm});
            skArc(sketch, "E160.2", {"start": v(-39.8, -41.07) * mm, "mid": v(-36.69, -38.99) * mm, "end": v(-33.76, -36.66) * mm});
            skArc(sketch, "E160.3", {"start": v(-39.8, -41.07) * mm, "mid": v(-36.68, -47.54) * mm, "end": v(-31.37, -52.4) * mm});
            skArc(sketch, "E160.4", {"start": v(-31.37, -52.4) * mm, "mid": v(-30.13, -52.27) * mm, "end": v(-28.9, -52.1) * mm});
            skArc(sketch, "E160.5", {"start": v(-30.82, -29.45) * mm, "mid": v(-32.6, -32.93) * mm, "end": v(-33.76, -36.66) * mm});
            skArc(sketch, "E160.6", {"start": v(-28.9, -52.1) * mm, "mid": v(-25.59, -49.94) * mm, "end": v(-22.64, -47.3) * mm});
            skArc(sketch, "E161.0", {"start": v(-42.8, -42.74) * mm, "mid": v(-40.28, -48.08) * mm, "end": v(-36.4, -52.52) * mm});
            skArc(sketch, "E161.1", {"start": v(-49.6, -45.51) * mm, "mid": v(-46.14, -44.26) * mm, "end": v(-42.8, -42.74) * mm});
            skArc(sketch, "E161.2", {"start": v(-37.22, -52.49) * mm, "mid": v(-36.8, -52.5) * mm, "end": v(-36.4, -52.52) * mm});
            skArc(sketch, "E161.3", {"start": v(-46.22, -50.84) * mm, "mid": v(-41.76, -51.9) * mm, "end": v(-37.22, -52.49) * mm});
            skArc(sketch, "E161.4", {"start": v(-49.6, -45.51) * mm, "mid": v(-48.18, -48.35) * mm, "end": v(-46.22, -50.84) * mm});
            skArc(sketch, "E162.0", {"start": v(-55.3, -46.9) * mm, "mid": v(-54.22, -46.7) * mm, "end": v(-53.15, -46.47) * mm});
            skArc(sketch, "E162.1", {"start": v(-55.3, -46.9) * mm, "mid": v(-53.7, -47.78) * mm, "end": v(-52.08, -48.59) * mm});
            skArc(sketch, "E162.2", {"start": v(-53.15, -46.47) * mm, "mid": v(-52.65, -47.55) * mm, "end": v(-52.08, -48.59) * mm});
            skSolve(sketch);
        }
        {
            var Q0;
            Q0 = qSketchRegion(id + "F3", true);
            extrude(context, id + "F4", {"entities" : qUnion([Q0]), "operationType" : NewBodyOperationType.REMOVE, "endBound" : BoundingType.SYMMETRIC, "oppositeDirection" : true, "depth" : 127 * mm});
        }
        {
            var Q0;
            Q0=qCreatedBy(makeId("Right.planeOp"),FACE);
            var sketch = newSketch(context, id + "F5", { "sketchPlane" : qUnion([Q0])});
            skCircle(sketch, "E163", {"center": v(0, -15.35) * mm, "radius": 5.72 * mm});
            skSolve(sketch);
        }
        {
            var Q0;
            Q0=qCreatedBy(makeId("Right.planeOp"),FACE);
            var sketch = newSketch(context, id + "F6", { "sketchPlane" : qUnion([Q0])});
            skCircle(sketch, "E164", {"center": v(0, -15.2) * mm, "radius": 4.5 * mm});
            skSolve(sketch);
        }
        {
            var Q0;
            Q0 = qSketchRegion(id + "F5", true);
            extrude(context, id + "F7", {"entities" : qUnion([Q0]), "operationType" : NewBodyOperationType.ADD, "depth" : 20 * mm});
        }
        {
            var Q0;
            Q0 = qSketchRegion(id + "F6", true);
            extrude(context, id + "F8", {"entities" : qUnion([Q0]), "operationType" : NewBodyOperationType.REMOVE, "depth" : 20 * mm});
        }
    });
